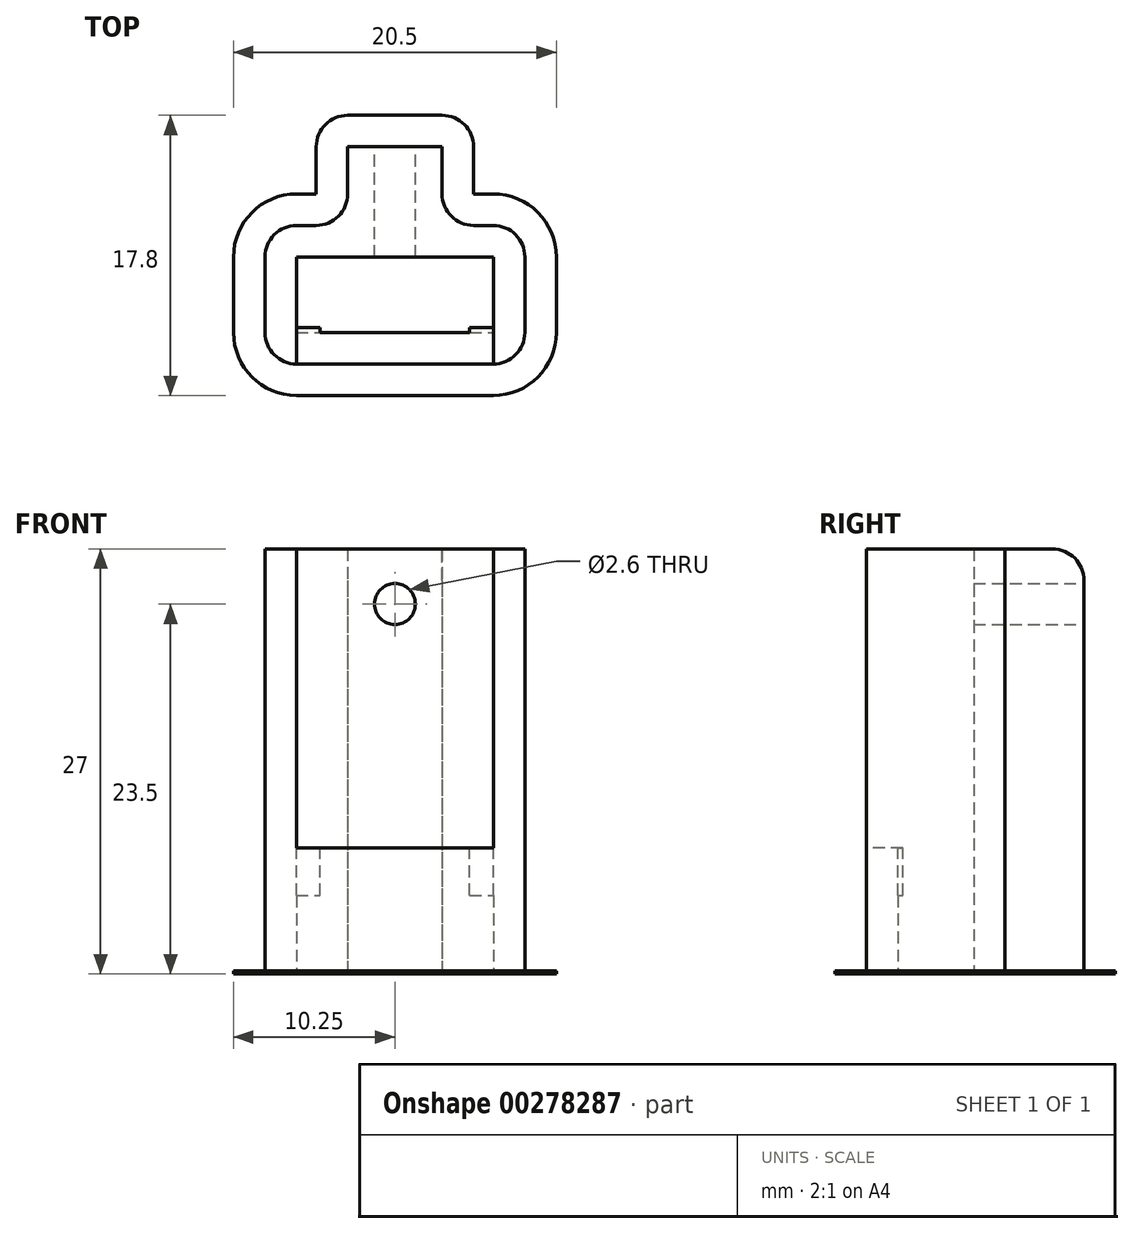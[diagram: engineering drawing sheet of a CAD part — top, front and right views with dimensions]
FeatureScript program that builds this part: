
annotation { "Feature Type Name" : "Feature", "Feature Type Description" : "" }
export const myFeature = defineFeature(function(context is Context, id is Id, definition is map)
    precondition{}
    {
        {
            var Q0;
            Q0=qCreatedBy(makeId("Top.planeOp"),FACE);
            var sketch = newSketch(context, id + "F0", { "sketchPlane" : qUnion([Q0])});
            skLineSegment(sketch, "E0.bottom", {"start": v(0, 0) * mm, "end": v(12, 0) * mm, "construction": true});
            skLineSegment(sketch, "E0.top", {"start": v(0, 4.5) * mm, "end": v(12, 4.5) * mm, "construction": true});
            skLineSegment(sketch, "E0.left", {"start": v(0, 0) * mm, "end": v(0, 4.5) * mm, "construction": true});
            skLineSegment(sketch, "E0.right", {"start": v(12, 0) * mm, "end": v(12, 4.5) * mm, "construction": true});
            skLineSegment(sketch, "E1.bottom", {"start": v(-0.25, 4.65) * mm, "end": v(12.25, 4.65) * mm});
            skLineSegment(sketch, "E1.top", {"start": v(-0.25, -0.15) * mm, "end": v(12.25, -0.15) * mm});
            skLineSegment(sketch, "E1.left", {"start": v(-0.25, 4.65) * mm, "end": v(-0.25, -0.15) * mm});
            skLineSegment(sketch, "E1.right", {"start": v(12.25, 4.65) * mm, "end": v(12.25, -0.15) * mm});
            skLineSegment(sketch, "E2", {"start": v(-2.25, 6.65) * mm, "end": v(-2.25, -2.15) * mm});
            skLineSegment(sketch, "E3", {"start": v(-2.25, -2.15) * mm, "end": v(14.25, -2.15) * mm});
            skLineSegment(sketch, "E4", {"start": v(14.25, -2.15) * mm, "end": v(14.25, 6.65) * mm});
            skLineSegment(sketch, "E5", {"start": v(3, 11.65) * mm, "end": v(9, 11.65) * mm});
            skLineSegment(sketch, "E6", {"start": v(-2.25, 6.65) * mm, "end": v(3, 6.65) * mm});
            skLineSegment(sketch, "E7", {"start": v(3, 6.65) * mm, "end": v(3, 11.65) * mm});
            skLineSegment(sketch, "E8", {"start": v(9, 11.65) * mm, "end": v(9, 6.65) * mm});
            skLineSegment(sketch, "E9", {"start": v(9, 6.65) * mm, "end": v(14.25, 6.65) * mm});
            skSolve(sketch);
        }
        {
            var Q0;
            Q0 = qSketchRegion(id + "F0", true);
            extrude(context, id + "F1", {"entities" : qUnion([Q0]), "depth" : 27 * mm, "offsetDistance" : 25 * mm});
        }
        {
            var Q0;
            Q0=makeQuery(id+"F1.opExtrude","CAP_FACE",FACE,{"disambiguationData":[OSD([sQuery(id+"F0.wireOp",EDGE,"E1.bottom"),sQuery(id+"F0.wireOp",EDGE,"E1.top"),sQuery(id+"F0.wireOp",EDGE,"E1.left"),sQuery(id+"F0.wireOp",EDGE,"E1.right"),sQuery(id+"F0.wireOp",EDGE,"E2"),sQuery(id+"F0.wireOp",EDGE,"E3"),sQuery(id+"F0.wireOp",EDGE,"E4"),sQuery(id+"F0.wireOp",EDGE,"E5"),sQuery(id+"F0.wireOp",EDGE,"E6"),sQuery(id+"F0.wireOp",EDGE,"E7"),sQuery(id+"F0.wireOp",EDGE,"E8"),sQuery(id+"F0.wireOp",EDGE,"E9")])],"isStart":false});
            var sketch = newSketch(context, id + "F2", { "sketchPlane" : qUnion([Q0])});
            skLineSegment(sketch, "E10.bottom", {"start": v(-0.25, 4.65) * mm, "end": v(12.25, 4.65) * mm});
            skLineSegment(sketch, "E10.top", {"start": v(-0.25, -2.15) * mm, "end": v(12.25, -2.15) * mm});
            skLineSegment(sketch, "E10.left", {"start": v(-0.25, 4.65) * mm, "end": v(-0.25, -2.15) * mm});
            skLineSegment(sketch, "E10.right", {"start": v(12.25, 4.65) * mm, "end": v(12.25, -2.15) * mm});
            skSolve(sketch);
        }
        {
            var Q0;
            Q0 = qSketchRegion(id + "F2", true);
            extrude(context, id + "F3", {"entities" : qUnion([Q0]), "operationType" : NewBodyOperationType.REMOVE, "oppositeDirection" : true, "depth" : 19 * mm, "offsetDistance" : 25 * mm});
        }
        {
            var Q0;
            Q0=makeQuery(id+"F3.boolean.opBoolean","COPY",FACE,{"derivedFrom":makeQuery(id+"F3.opExtrude","CAP_FACE",FACE,{"disambiguationData":[OSD([sQuery(id+"F2.wireOp",EDGE,"E10.bottom"),sQuery(id+"F2.wireOp",EDGE,"E10.top"),sQuery(id+"F2.wireOp",EDGE,"E10.left"),sQuery(id+"F2.wireOp",EDGE,"E10.right")])],"isStart":false})});
            var sketch = newSketch(context, id + "F4", { "sketchPlane" : qUnion([Q0])});
            skLineSegment(sketch, "E11.bottom", {"start": v(-0.25, -0.15) * mm, "end": v(1.25, -0.15) * mm});
            skLineSegment(sketch, "E11.top", {"start": v(-0.25, 0.15) * mm, "end": v(1.25, 0.15) * mm});
            skLineSegment(sketch, "E11.left", {"start": v(-0.25, -0.15) * mm, "end": v(-0.25, 0.15) * mm});
            skLineSegment(sketch, "E11.right", {"start": v(1.25, -0.15) * mm, "end": v(1.25, 0.15) * mm});
            skLineSegment(sketch, "E12.bottom", {"start": v(12.25, -0.15) * mm, "end": v(10.75, -0.15) * mm});
            skLineSegment(sketch, "E12.top", {"start": v(12.25, 0.15) * mm, "end": v(10.75, 0.15) * mm});
            skLineSegment(sketch, "E12.left", {"start": v(12.25, -0.15) * mm, "end": v(12.25, 0.15) * mm});
            skLineSegment(sketch, "E12.right", {"start": v(10.75, -0.15) * mm, "end": v(10.75, 0.15) * mm});
            skSolve(sketch);
        }
        {
            var Q0;
            Q0 = qSketchRegion(id + "F4", true);
            extrude(context, id + "F5", {"entities" : qUnion([Q0]), "operationType" : NewBodyOperationType.ADD, "oppositeDirection" : true, "depth" : 3 * mm, "offsetDistance" : 25 * mm});
        }
        {
            var Q0;
            Q0=makeQuery(id+"F1.opExtrude","SWEPT_FACE",FACE,{"disambiguationData":[OSD([sQuery(id+"F0.wireOp",EDGE,"E5")])]});
            var sketch = newSketch(context, id + "F6", { "sketchPlane" : qUnion([Q0])});
            skCircle(sketch, "E13", {"center": v(-6, 23.5) * mm, "radius": 1.3 * mm});
            skLineSegment(sketch, "E14", {"start": v(-6, 27) * mm, "end": v(-6, 0) * mm, "construction": true});
            skSolve(sketch);
        }
        {
            var Q0;
            Q0 = qSketchRegion(id + "F6", true);
            extrude(context, id + "F7", {"entities" : qUnion([Q0]), "operationType" : NewBodyOperationType.REMOVE, "endBound" : BoundingType.THROUGH_ALL, "oppositeDirection" : true, "depth" : 25 * mm, "offsetDistance" : 25 * mm});
        }
        {
            var Q0;
            Q0=makeQuery(id+"F1.opExtrude","SWEPT_EDGE",EDGE,{"disambiguationData":[OSD([sQuery(id+"F0.wireOp",EDGE,"E8"),sQuery(id+"F0.wireOp",EDGE,"E9")])]});
            var Q1;
            Q1=makeQuery(id+"F1.opExtrude","SWEPT_EDGE",EDGE,{"disambiguationData":[OSD([sQuery(id+"F0.wireOp",EDGE,"E6"),sQuery(id+"F0.wireOp",EDGE,"E7")])]});
            var Q2;
            Q2=makeQuery(id+"F1.opExtrude","SWEPT_EDGE",EDGE,{"disambiguationData":[OSD([sQuery(id+"F0.wireOp",EDGE,"E2"),sQuery(id+"F0.wireOp",EDGE,"E6")])]});
            var Q3;
            Q3=makeQuery(id+"F1.opExtrude","SWEPT_EDGE",EDGE,{"disambiguationData":[OSD([sQuery(id+"F0.wireOp",EDGE,"E2"),sQuery(id+"F0.wireOp",EDGE,"E3")])]});
            var Q4;
            Q4=makeQuery(id+"F1.opExtrude","SWEPT_EDGE",EDGE,{"disambiguationData":[OSD([sQuery(id+"F0.wireOp",EDGE,"E4"),sQuery(id+"F0.wireOp",EDGE,"E9")])]});
            var Q5;
            Q5=makeQuery(id+"F1.opExtrude","SWEPT_EDGE",EDGE,{"disambiguationData":[OSD([sQuery(id+"F0.wireOp",EDGE,"E3"),sQuery(id+"F0.wireOp",EDGE,"E4")])]});
            var Q6;
            Q6=makeQuery(id+"F1.opExtrude","CAP_EDGE",EDGE,{"disambiguationData":[OSD([sQuery(id+"F0.wireOp",EDGE,"E5")])],"isStart":false});
            fillet(context, id + "F8", {"entities" : qUnion([Q0, Q1, Q2, Q3, Q4, Q5, Q6]), "radius" : 2 * mm, "tangentPropagation" : true, "allowEdgeOverflow" : false});
        }
        {
            var Q0;
            Q0=makeQuery(id+"F1.opExtrude","CAP_FACE",FACE,{"disambiguationData":[OSD([sQuery(id+"F0.wireOp",EDGE,"E1.bottom"),sQuery(id+"F0.wireOp",EDGE,"E1.top"),sQuery(id+"F0.wireOp",EDGE,"E1.left"),sQuery(id+"F0.wireOp",EDGE,"E1.right"),sQuery(id+"F0.wireOp",EDGE,"E2"),sQuery(id+"F0.wireOp",EDGE,"E3"),sQuery(id+"F0.wireOp",EDGE,"E4"),sQuery(id+"F0.wireOp",EDGE,"E5"),sQuery(id+"F0.wireOp",EDGE,"E6"),sQuery(id+"F0.wireOp",EDGE,"E7"),sQuery(id+"F0.wireOp",EDGE,"E8"),sQuery(id+"F0.wireOp",EDGE,"E9")])],"isStart":true});
            var sketch = newSketch(context, id + "F9", { "sketchPlane" : qUnion([Q0])});
            skLineSegment(sketch, "E15", {"start": v(-2.25, -4.65) * mm, "end": v(-2.25, 0.15) * mm});
            skLineSegment(sketch, "E16", {"start": v(-0.25, 2.15) * mm, "end": v(12.25, 2.15) * mm});
            skLineSegment(sketch, "E17", {"start": v(14.25, 0.15) * mm, "end": v(14.25, -4.65) * mm});
            skLineSegment(sketch, "E18", {"start": v(-0.25, -6.65) * mm, "end": v(1, -6.65) * mm});
            skLineSegment(sketch, "E19", {"start": v(3, -8.65) * mm, "end": v(3, -11.65) * mm});
            skLineSegment(sketch, "E20", {"start": v(3, -11.65) * mm, "end": v(9, -11.65) * mm});
            skLineSegment(sketch, "E21", {"start": v(9, -11.65) * mm, "end": v(9, -8.65) * mm});
            skLineSegment(sketch, "E22", {"start": v(11, -6.65) * mm, "end": v(12.25, -6.65) * mm});
            skArc(sketch, "E23", {"start": v(-0.25, 2.15) * mm, "mid": v(-1.66, 1.56) * mm, "end": v(-2.25, 0.15) * mm});
            skArc(sketch, "E24", {"start": v(14.25, 0.15) * mm, "mid": v(13.66, 1.56) * mm, "end": v(12.25, 2.15) * mm});
            skArc(sketch, "E25", {"start": v(12.25, -6.65) * mm, "mid": v(13.66, -6.06) * mm, "end": v(14.25, -4.65) * mm});
            skArc(sketch, "E26", {"start": v(11, -6.65) * mm, "mid": v(9.59, -7.24) * mm, "end": v(9, -8.65) * mm});
            skArc(sketch, "E27", {"start": v(3, -8.65) * mm, "mid": v(2.41, -7.24) * mm, "end": v(1, -6.65) * mm});
            skArc(sketch, "E28", {"start": v(-2.25, -4.65) * mm, "mid": v(-1.66, -6.06) * mm, "end": v(-0.25, -6.65) * mm});
            skLineSegment(sketch, "E29", {"start": v(-4.25, 0.15) * mm, "end": v(-4.25, -4.65) * mm});
            skLineSegment(sketch, "E30", {"start": v(-0.25, 4.15) * mm, "end": v(12.25, 4.15) * mm});
            skLineSegment(sketch, "E31", {"start": v(16.25, 0.15) * mm, "end": v(16.25, -4.65) * mm});
            skLineSegment(sketch, "E32", {"start": v(3, -13.65) * mm, "end": v(9, -13.65) * mm});
            skLineSegment(sketch, "E33", {"start": v(1, -8.65) * mm, "end": v(1, -11.65) * mm});
            skLineSegment(sketch, "E34", {"start": v(11, -8.65) * mm, "end": v(11, -11.65) * mm});
            skLineSegment(sketch, "E35", {"start": v(1, -8.65) * mm, "end": v(-0.25, -8.65) * mm});
            skLineSegment(sketch, "E36", {"start": v(11, -8.65) * mm, "end": v(12.25, -8.65) * mm});
            skArc(sketch, "E37", {"start": v(1, -11.65) * mm, "mid": v(1.59, -13.06) * mm, "end": v(3, -13.65) * mm});
            skArc(sketch, "E38", {"start": v(9, -13.65) * mm, "mid": v(10.41, -13.06) * mm, "end": v(11, -11.65) * mm});
            skArc(sketch, "E39", {"start": v(12.25, -8.65) * mm, "mid": v(15.08, -7.48) * mm, "end": v(16.25, -4.65) * mm});
            skArc(sketch, "E40", {"start": v(16.25, 0.15) * mm, "mid": v(15.08, 2.98) * mm, "end": v(12.25, 4.15) * mm});
            skArc(sketch, "E41", {"start": v(-0.25, 4.15) * mm, "mid": v(-3.08, 2.98) * mm, "end": v(-4.25, 0.15) * mm});
            skArc(sketch, "E42", {"start": v(-4.25, -4.65) * mm, "mid": v(-3.08, -7.48) * mm, "end": v(-0.25, -8.65) * mm});
            skSolve(sketch);
        }
        {
            var Q0;
            Q0 = qSketchRegion(id + "F9", true);
            extrude(context, id + "F10", {"entities" : qUnion([Q0]), "operationType" : NewBodyOperationType.ADD, "oppositeDirection" : true, "depth" : 0.2 * mm, "offsetDistance" : 25 * mm});
        }
    });
